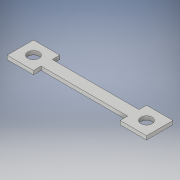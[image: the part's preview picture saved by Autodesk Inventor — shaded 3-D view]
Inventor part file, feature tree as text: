
AUTODESK INVENTOR PART (.ipt)
format: ipt  version: 2018 (Build 220112000, 112)  size: 138,752 bytes
history: native  units: in
note: dims shown in document units (in); Inventor stores cm internally (conversion verified against a paired STEP export)
features: extrude x3, sketch x3
ambient origin geometry x8: Origin, YZ Plane, XZ Plane, XY Plane, X Axis, Y Axis, Z Axis, Center Point
bodies: Solid1 (feature_tree)
feature tree (6):
  extrude  "Extrusion1"  Depth=1.4567in
  extrude  "Extrusion2"  Depth=0.2756in
  extrude  "Extrusion3"  TaperAngle=0.0deg  [1 undecoded]
  sketch  "Sketch1"  dims[d0=0.1181in d1=1.4567in]
  sketch  "Sketch2"  dims[d2=0.0394in d3=0.0in d4=0.2756in]
  sketch  "Sketch3"  dims[d5=0.2756in d6=0.0in d7=0.2756in d8=0.2756in d9=0.0in d12=0.0394in d13=0.0in d14=0.1181in d15=0.1181in d16=0.1181in d17=0.0in]
note: 1 required parameter value undecoded (feature->parameter linkage not recoverable at this tier; creation-order binding heuristic only, values carry confidence <= 0.55)
